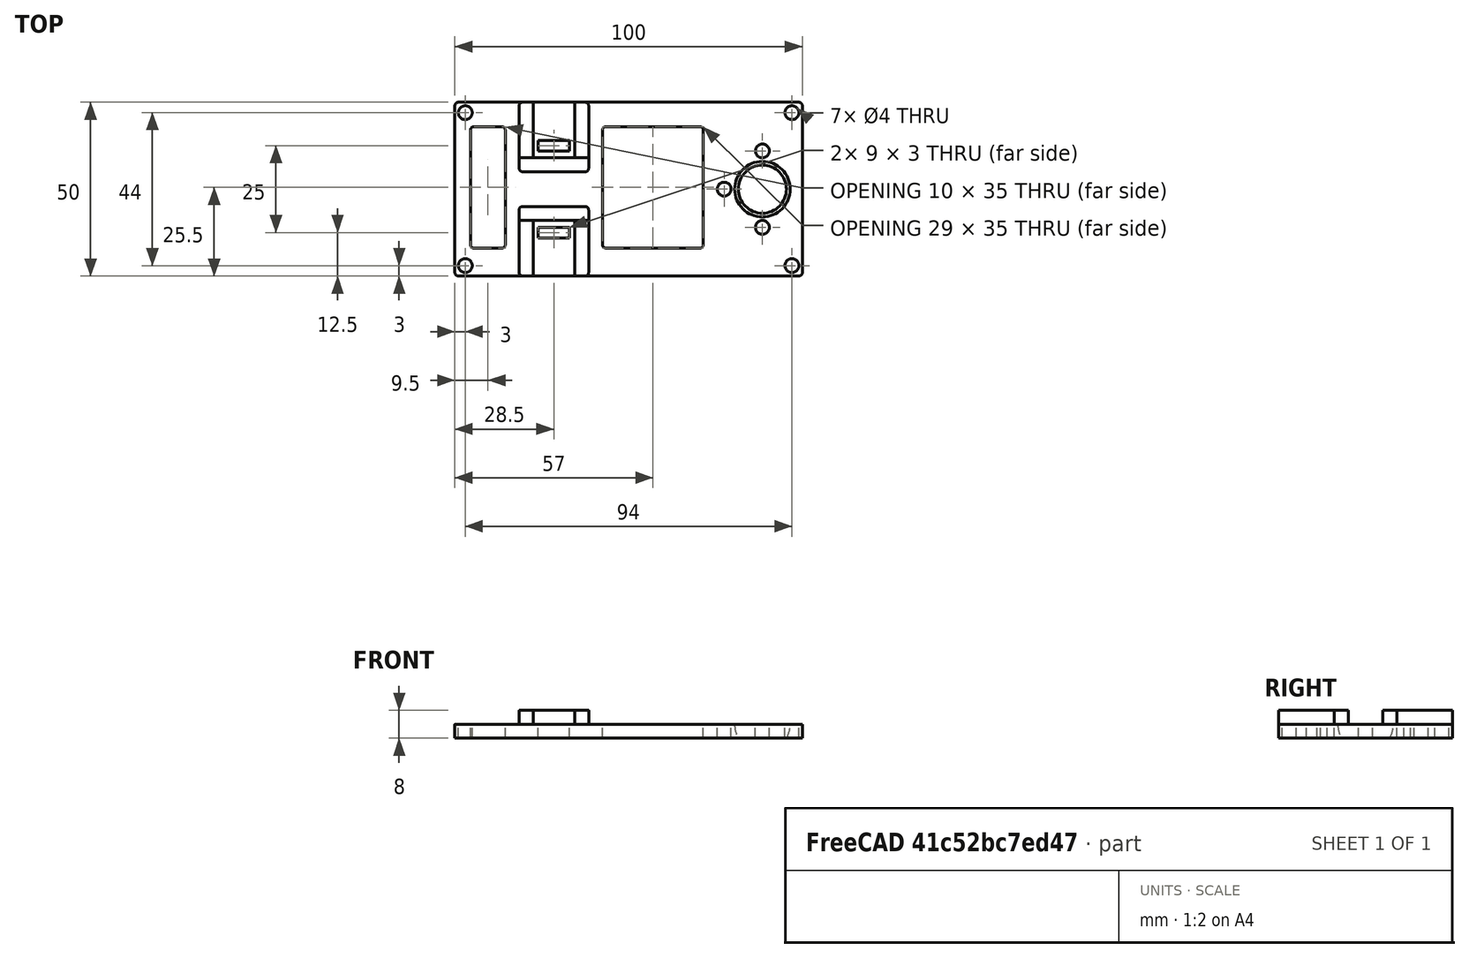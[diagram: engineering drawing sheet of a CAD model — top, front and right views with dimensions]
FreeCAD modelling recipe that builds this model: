
FCSTD DOCUMENT  (FreeCAD 0.20R29603 (Git))
Label: plate
License: All rights reserved
LicenseURL: http://en.wikipedia.org/wiki/All_rights_reserved
objects: Part::Cut×12, Part::Box×11, Part::Fillet×9, Part::Cylinder×7, Part::Sphere×1
note: 40 computed .brp shape members not serialized (recipe doc carries the construction recipe); baked Part::Feature solids carry a one-line shape summary decoded from their .brp

FEATURE [Part::Box] Box  label="Cube"
  AttacherType = Attacher::AttachEngine3D
  Height = 4
  Length = 100
  Width = 50
FEATURE [Part::Cylinder] Cylinder  label="corner 1"
  Angle = 360
  AttacherType = Attacher::AttachEngine3D
  FirstAngle = 0
  Height = 4
  Placement = pos=(3,3,0) rot=(0,0,1;0rad)
  Radius = 2
  SecondAngle = 0
FEATURE [Part::Cylinder] Cylinder001  label="corner 2"
  Angle = 360
  AttacherType = Attacher::AttachEngine3D
  FirstAngle = 0
  Height = 4
  Placement = pos=(3,47,0) rot=(0,0,1;0rad)
  Radius = 2
  SecondAngle = 0
FEATURE [Part::Cylinder] Cylinder002  label="corner 3"
  Angle = 360
  AttacherType = Attacher::AttachEngine3D
  FirstAngle = 0
  Height = 4
  Placement = pos=(97,3,0) rot=(0,0,1;0rad)
  Radius = 2
  SecondAngle = 0
FEATURE [Part::Cylinder] Cylinder003  label="corner 4"
  Angle = 360
  AttacherType = Attacher::AttachEngine3D
  FirstAngle = 0
  Height = 4
  Placement = pos=(97,47,0) rot=(0,0,1;0rad)
  Radius = 2
  SecondAngle = 0
FEATURE [Part::Cut] Cut
  Base = -> Box
  Tool = -> Cylinder
FEATURE [Part::Cut] Cut001
  Base = -> Cut
  Tool = -> Cylinder003
FEATURE [Part::Cut] Cut002
  Base = -> Cut001
  Tool = -> Cylinder002
FEATURE [Part::Cut] Cut003
  Base = -> Cut002
  Placement = pos=(-22.5,0,0) rot=(0,0,1;0rad)
  Tool = -> Cylinder001
FEATURE [Part::Box] Box001  label="Cube001"
  AttacherType = Attacher::AttachEngine3D
  Height = 4
  Length = 20
  Placement = pos=(-4,16,4) rot=(0,0,1;0rad)
  Width = 4
FEATURE [Part::Box] Box002  label="Cube002"
  AttacherType = Attacher::AttachEngine3D
  Height = 4
  Length = 4
  Placement = pos=(-4,0,4) rot=(0,0,1;0rad)
  Width = 16
FEATURE [Part::Box] Box003  label="Cube003"
  AttacherType = Attacher::AttachEngine3D
  Height = 4
  Length = 4
  Placement = pos=(12,0,4) rot=(0,0,1;0rad)
  Width = 16
FEATURE [Part::Box] Box004  label="Cube004"
  AttacherType = Attacher::AttachEngine3D
  Height = 4
  Length = 4
  Placement = pos=(-4,34,4) rot=(0,0,1;0rad)
  Width = 16
FEATURE [Part::Box] Box005  label="Cube005"
  AttacherType = Attacher::AttachEngine3D
  Height = 4
  Length = 4
  Placement = pos=(12,34,4) rot=(0,0,1;0rad)
  Width = 16
FEATURE [Part::Box] Box006  label="Cube006"
  AttacherType = Attacher::AttachEngine3D
  Height = 4
  Length = 20
  Placement = pos=(-4,30,4) rot=(0,0,1;0rad)
  Width = 4
FEATURE [Part::Box] Box007  label="Cube007"
  AttacherType = Attacher::AttachEngine3D
  Height = 4
  Length = 9
  Placement = pos=(1.5,11,0) rot=(0,0,1;0rad)
  Width = 3
FEATURE [Part::Box] Box008  label="Cube008"
  AttacherType = Attacher::AttachEngine3D
  Height = 4
  Length = 9
  Placement = pos=(1.5,36,0) rot=(0,0,1;0rad)
  Width = 3
FEATURE [Part::Box] Box009  label="Cube009"
  AttacherType = Attacher::AttachEngine3D
  Height = 4
  Length = 10
  Placement = pos=(-18,8,0) rot=(0,0,1;0rad)
  Width = 35
FEATURE [Part::Sphere] Sphere
  Angle1 = -90
  Angle2 = 90
  Angle3 = 360
  AttacherType = Attacher::AttachEngine3D
  Placement = pos=(66,25,4) rot=(0,0,1;0rad)
  Radius = 8
FEATURE [Part::Cut] Cut004
  Base = -> Cut003
  Tool = -> Box007
FEATURE [Part::Cut] Cut005
  Base = -> Cut004
  Tool = -> Box008
FEATURE [Part::Cut] Cut006
  Base = -> Cut005
  Tool = -> Box009
FEATURE [Part::Cylinder] Cylinder004  label="Cylinder"
  Angle = 360
  AttacherType = Attacher::AttachEngine3D
  FirstAngle = 0
  Height = 4
  Placement = pos=(55,25,0) rot=(0,0,1;0rad)
  Radius = 2
  SecondAngle = 0
FEATURE [Part::Cylinder] Cylinder005  label="Cylinder001"
  Angle = 360
  AttacherType = Attacher::AttachEngine3D
  FirstAngle = 0
  Height = 4
  Placement = pos=(66,14,0) rot=(0,0,1;0rad)
  Radius = 2
  SecondAngle = 0
FEATURE [Part::Cylinder] Cylinder006  label="Cylinder002"
  Angle = 360
  AttacherType = Attacher::AttachEngine3D
  FirstAngle = 0
  Height = 4
  Placement = pos=(66,36,0) rot=(0,0,1;0rad)
  Radius = 2
  SecondAngle = 0
FEATURE [Part::Box] Box010  label="Cube010"
  AttacherType = Attacher::AttachEngine3D
  Height = 4
  Length = 29
  Placement = pos=(20,8,0) rot=(0,0,1;0rad)
  Width = 35
FEATURE [Part::Cut] Cut007
  Base = -> Cut006
  Tool = -> Cylinder005
FEATURE [Part::Cut] Cut008
  Base = -> Cut007
  Tool = -> Cylinder004
FEATURE [Part::Cut] Cut009
  Base = -> Cut008
  Tool = -> Box010
FEATURE [Part::Cut] Cut010
  Base = -> Cut009
  Tool = -> Cylinder006
FEATURE [Part::Cut] Cut011
  Base = -> Cut010
  Tool = -> Sphere
FEATURE [Part::Fillet] Fillet
  Base = -> Cut011
  Edges = 4 edges r=1: [Edge1,Edge3,Edge6,Edge35]
FEATURE [Part::Fillet] Fillet001
  Base = -> Fillet
  Edges = 8 edges r=1: [Edge74,Edge75,Edge76,Edge77,Edge92,Edge93,Edge94,Edge95]
FEATURE [Part::Fillet] Fillet002
  Base = -> Box003
  Edges = 1 edges r=1: [Edge5]
FEATURE [Part::Fillet] Fillet003
  Base = -> Box001
  Edges = 1 edges r=1: [Edge7]
FEATURE [Part::Fillet] Fillet004
  Base = -> Box002
  Edges = 1 edges r=1: [Edge1]
FEATURE [Part::Fillet] Fillet005
  Base = -> Box006
  Edges = 2 edges r=1: [Edge1,Edge5]
FEATURE [Part::Fillet] Fillet006
  Base = -> Box005
  Edges = 1 edges r=1: [Edge7]
FEATURE [Part::Fillet] Fillet007
  Base = -> Fillet003
  Edges = 1 edges r=1: [Edge15]
FEATURE [Part::Fillet] Fillet008
  Base = -> Box004
  Edges = 1 edges r=1: [Edge3]
